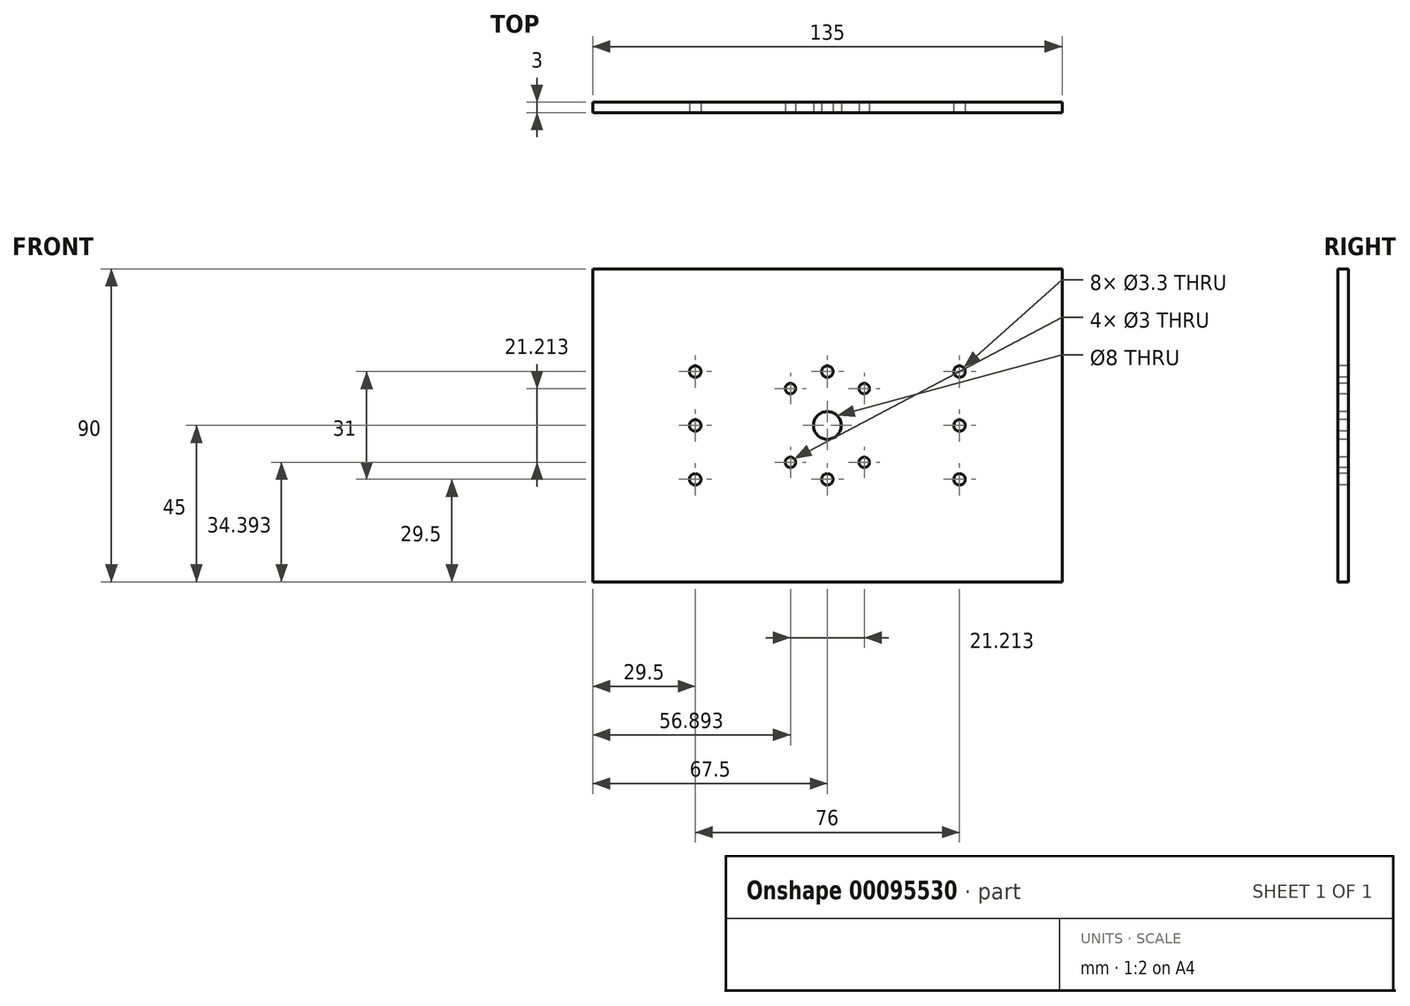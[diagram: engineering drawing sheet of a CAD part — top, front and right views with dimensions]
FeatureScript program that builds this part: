
annotation { "Feature Type Name" : "Feature", "Feature Type Description" : "" }
export const myFeature = defineFeature(function(context is Context, id is Id, definition is map)
    precondition{}
    {
        {
            var Q0;
            Q0=qCreatedBy(makeId("Front.planeOp"),FACE);
            var sketch = newSketch(context, id + "F0", { "sketchPlane" : qUnion([Q0])});
            skLineSegment(sketch, "E0.bottom", {"start": v(67.5, -45) * mm, "end": v(-67.5, -45) * mm});
            skLineSegment(sketch, "E0.top", {"start": v(67.5, 45) * mm, "end": v(-67.5, 45) * mm});
            skLineSegment(sketch, "E0.left", {"start": v(67.5, -45) * mm, "end": v(67.5, 45) * mm});
            skLineSegment(sketch, "E0.right", {"start": v(-67.5, -45) * mm, "end": v(-67.5, 45) * mm});
            skPoint(sketch, "E0.middle", {"position": v(0, 0) * mm});
            skSolve(sketch);
        }
        {
            var Q0;
            Q0 = qSketchRegion(id + "F0", true);
            extrude(context, id + "F1", {"entities" : qUnion([Q0]), "depth" : 3 * mm});
        }
        {
            var Q0;
            Q0=makeQuery(id+"F1.opExtrude","CAP_FACE",FACE,{"disambiguationData":[OSD([sQuery(id+"F0.wireOp",EDGE,"E0.bottom"),sQuery(id+"F0.wireOp",EDGE,"E0.top"),sQuery(id+"F0.wireOp",EDGE,"E0.left"),sQuery(id+"F0.wireOp",EDGE,"E0.right")])],"isStart":false});
            var sketch = newSketch(context, id + "F2", { "sketchPlane" : qUnion([Q0])});
            skCircle(sketch, "E1", {"center": v(0, 15.5) * mm, "radius": 1.65 * mm});
            skCircle(sketch, "E2", {"center": v(0, -15.5) * mm, "radius": 1.65 * mm});
            skCircle(sketch, "E3", {"center": v(38, 0) * mm, "radius": 1.65 * mm});
            skCircle(sketch, "E4", {"center": v(-38, 0) * mm, "radius": 1.65 * mm});
            skCircle(sketch, "E5", {"center": v(-38, 15.5) * mm, "radius": 1.65 * mm});
            skCircle(sketch, "E6", {"center": v(-38, -15.5) * mm, "radius": 1.65 * mm});
            skCircle(sketch, "E7", {"center": v(38, 15.5) * mm, "radius": 1.65 * mm});
            skCircle(sketch, "E8", {"center": v(38, -15.5) * mm, "radius": 1.65 * mm});
            skCircle(sketch, "E9", {"center": v(10.6, 10.6) * mm, "radius": 1.5 * mm});
            skCircle(sketch, "E10", {"center": v(-10.6, -10.6) * mm, "radius": 1.5 * mm});
            skCircle(sketch, "E11", {"center": v(-10.6, 10.6) * mm, "radius": 1.5 * mm});
            skCircle(sketch, "E12", {"center": v(10.6, -10.6) * mm, "radius": 1.5 * mm});
            skCircle(sketch, "E13", {"center": v(0, 0) * mm, "radius": 4 * mm});
            skSolve(sketch);
        }
        {
            var Q0;
            Q0 = qSketchRegion(id + "F2", true);
            extrude(context, id + "F3", {"entities" : qUnion([Q0]), "operationType" : NewBodyOperationType.REMOVE, "endBound" : BoundingType.THROUGH_ALL, "oppositeDirection" : true, "depth" : 25 * mm});
        }
    });
